FCSTD DOCUMENT  (FreeCAD 1.0R38806 (Git))
Label: restriccion
License: All rights reserved
LicenseURL: https://en.wikipedia.org/wiki/All_rights_reserved
objects: Sketcher::SketchObject×1
note: 2 computed .brp shape members not serialized (recipe doc carries the construction recipe); baked Part::Feature solids carry a one-line shape summary decoded from their .brp

FEATURE [Sketcher::SketchObject] Sketch
  ArcFitTolerance = 1e-06
  FullyConstrained = false
  MakeInternals = false
  sketch-geometry (5):
    g0: LineSegment StartX=0 StartY=0 StartZ=0 EndX=0 EndY=22.5041 EndZ=0
    g1: LineSegment StartX=0 StartY=22.5041 StartZ=0 EndX=32.4973 EndY=55.0014 EndZ=0
    g2: LineSegment StartX=32.4973 StartY=55.0014 StartZ=0 EndX=57.8954 EndY=29.6034 EndZ=0
    g3: LineSegment StartX=57.8954 StartY=29.6034 StartZ=0 EndX=57.8954 EndY=0 EndZ=0
    g4: LineSegment StartX=57.8954 StartY=0 StartZ=0 EndX=0 EndY=0 EndZ=0
  constraints (11):
    c: Coincident(g-1,g0)
    c: PointOnObject(g0,g-2)
    c: Coincident(g0,g1)
    c: Coincident(g1,g2)
    c: Coincident(g2,g3)
    c: PointOnObject(g3,g-1)
    c: Vertical(g3)
    c: Coincident(g3,g4)
    c: Coincident(g4,g0)
    c: Angle(g0,g1) = 2.35619
    c: Angle(g2,g3) = 2.35619
